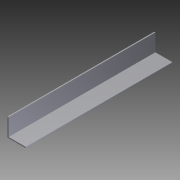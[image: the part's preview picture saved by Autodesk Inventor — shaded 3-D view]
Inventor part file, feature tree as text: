
AUTODESK INVENTOR PART (.ipt)
format: ipt  version: 2012 (Build 160160000, 160)  size: 74,240 bytes
history: native  units: in
note: dims shown in document units (in); Inventor stores cm internally (conversion verified against a paired STEP export)
features: extrude x1, sketch x1
ambient origin geometry x8: Origin, YZ Plane, XZ Plane, XY Plane, X Axis, Y Axis, Z Axis, Center Point
bodies: Solid1 (feature_tree)
feature tree (2):
  extrude  "Extrusion1"  Depth=1.0in
  sketch  "Sketch1"  dims[d0=1.0in d1=1.0in d2=0.0625in d3=0.0625in d4=8.0in d5=0.0in]
